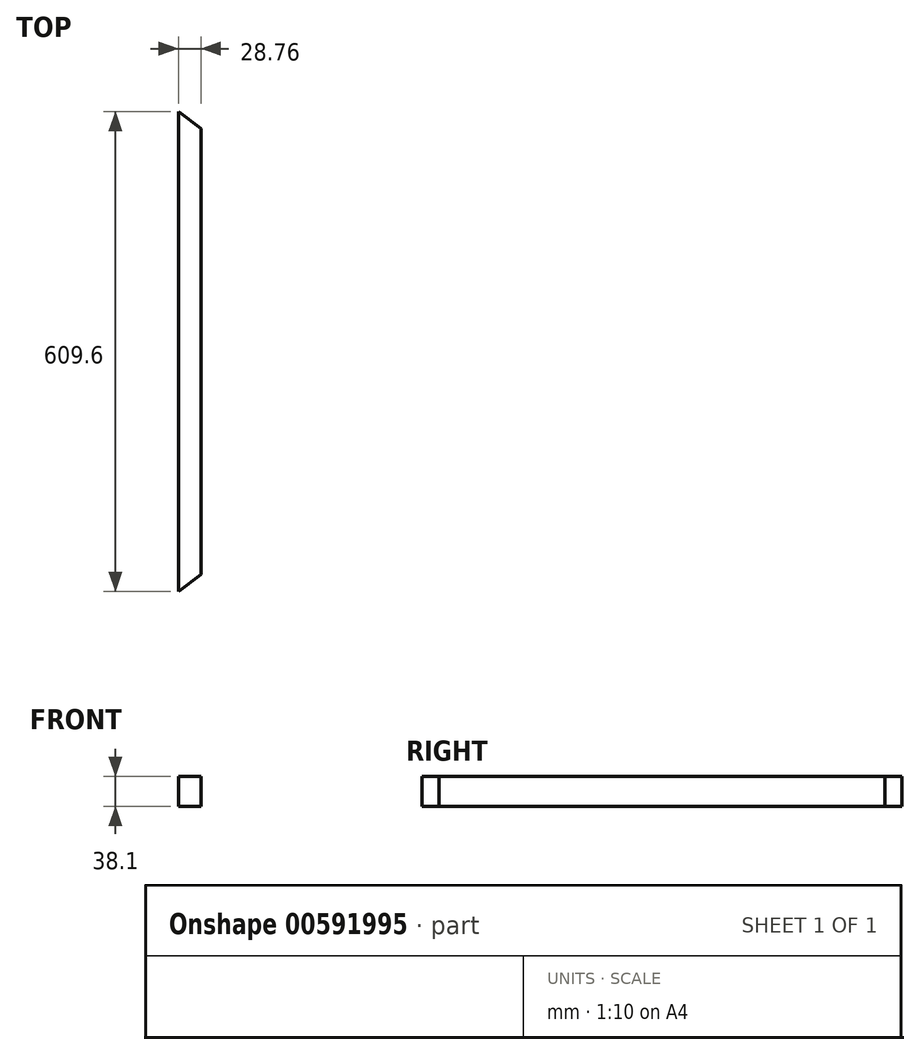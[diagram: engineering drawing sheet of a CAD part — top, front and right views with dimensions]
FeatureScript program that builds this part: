
annotation { "Feature Type Name" : "Feature", "Feature Type Description" : "" }
export const myFeature = defineFeature(function(context is Context, id is Id, definition is map)
    precondition{}
    {
        {
            var Q0;
            Q0=qCreatedBy(makeId("Top.planeOp"),FACE);
            var sketch = newSketch(context, id + "F0", { "sketchPlane" : qUnion([Q0])});
            skLineSegment(sketch, "E0", {"start": v(0, 0) * mm, "end": v(0, 609.6) * mm});
            skPoint(sketch, "E1.endSnap0", {"position": v(0, 304.8) * mm});
            skLineSegment(sketch, "E2", {"start": v(28.76, 304.03) * mm, "end": v(28.76, 588.08) * mm});
            skLineSegment(sketch, "E3", {"start": v(28.76, 304.03) * mm, "end": v(28.76, 21.52) * mm});
            skLineSegment(sketch, "E4", {"start": v(0, 609.6) * mm, "end": v(28.76, 588.08) * mm});
            skLineSegment(sketch, "E5", {"start": v(28.76, 21.52) * mm, "end": v(0, 0) * mm});
            skSolve(sketch);
        }
        {
            var Q0;
            Q0 = qSketchRegion(id + "F0", true);
            extrude(context, id + "F1", {"entities" : qUnion([Q0]), "depth" : 38.1 * mm, "offsetDistance" : 25.4 * mm});
        }
    });
